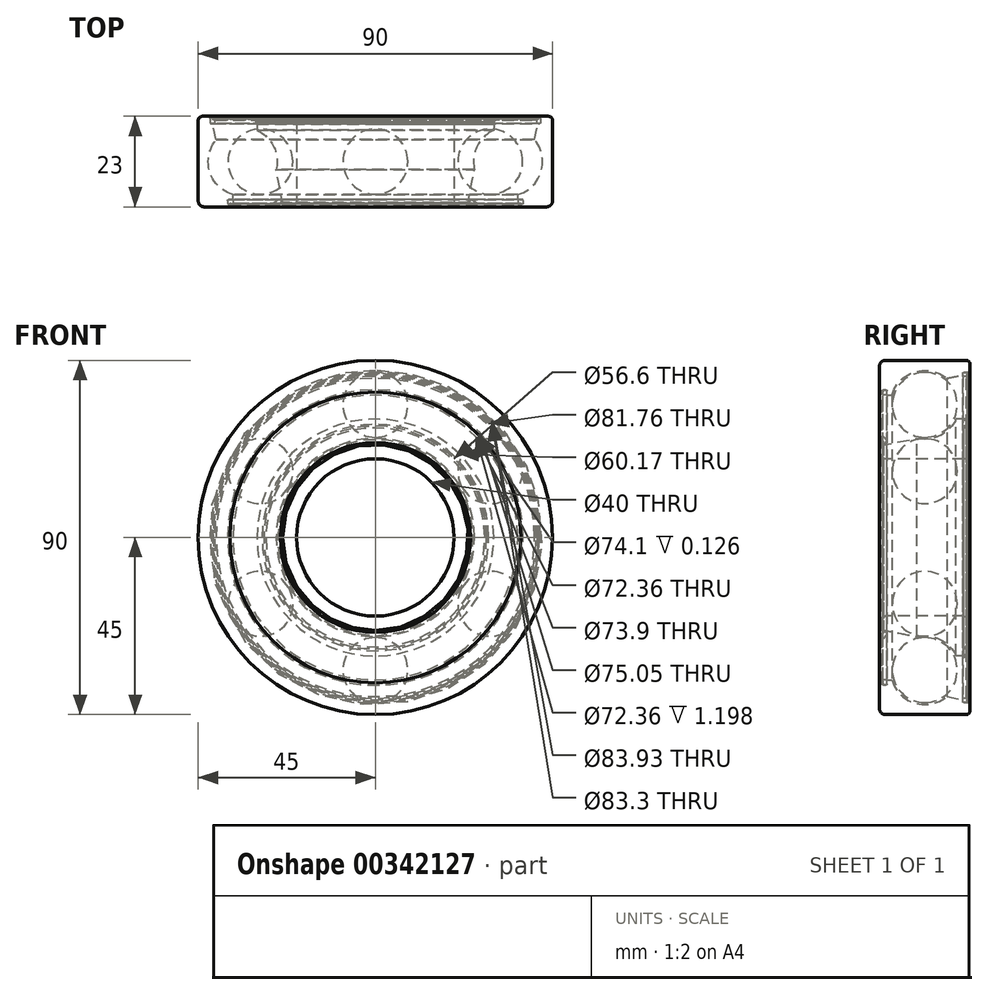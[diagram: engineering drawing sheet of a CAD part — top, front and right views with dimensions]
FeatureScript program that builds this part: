
annotation { "Feature Type Name" : "Feature", "Feature Type Description" : "" }
export const myFeature = defineFeature(function(context is Context, id is Id, definition is map)
    precondition{}
    {
        {
            var Q0;
            Q0=qCreatedBy(makeId("Right.planeOp"),FACE);
            var sketch = newSketch(context, id + "F0", { "sketchPlane" : qUnion([Q0])});
            skLineSegment(sketch, "E0", {"start": v(0, 0) * mm, "end": v(11.5, 0) * mm, "construction": true});
            skLineSegment(sketch, "E1", {"start": v(0, 0) * mm, "end": v(-11.5, 0) * mm, "construction": true});
            skLineSegment(sketch, "E2", {"start": v(-11.5, 0) * mm, "end": v(-11.5, 20) * mm, "construction": true});
            skLineSegment(sketch, "E3", {"start": v(-11.5, 37.05) * mm, "end": v(-11.5, 45) * mm});
            skLineSegment(sketch, "E4", {"start": v(-11.5, 20) * mm, "end": v(11.5, 20) * mm});
            skLineSegment(sketch, "E5", {"start": v(11.5, 45) * mm, "end": v(-11.5, 45) * mm});
            skLineSegment(sketch, "E6", {"start": v(11.5, 41.75) * mm, "end": v(11.5, 45) * mm});
            skLineSegment(sketch, "E7", {"start": v(0, 0) * mm, "end": v(0, 33.7) * mm, "construction": true});
            skLineSegment(sketch, "E8", {"start": v(0, 33.7) * mm, "end": v(28.28, 0) * mm, "construction": true});
            skArc(sketch, "E9", {"start": v(-10, 45) * mm, "mid": v(-11.06, 44.56) * mm, "end": v(-11.5, 43.5) * mm});
            skArc(sketch, "E10", {"start": v(-11.5, 21.5) * mm, "mid": v(-11.06, 20.44) * mm, "end": v(-10, 20) * mm});
            skArc(sketch, "E11", {"start": v(10, 20) * mm, "mid": v(11.06, 20.44) * mm, "end": v(11.5, 21.5) * mm});
            skArc(sketch, "E12", {"start": v(11.5, 44) * mm, "mid": v(11.2, 44.7) * mm, "end": v(10.5, 45) * mm});
            skCircle(sketch, "E13", {"center": v(0, 33.7) * mm, "radius": 8.75 * mm});
            skLineSegment(sketch, "E14", {"start": v(0, 33.7) * mm, "end": v(0, 42.46) * mm, "construction": true});
            skLineSegment(sketch, "E15", {"start": v(11.5, 27.8) * mm, "end": v(10.5, 27.8) * mm});
            skLineSegment(sketch, "E16", {"start": v(11.4, 41.65) * mm, "end": v(11.34, 41.65) * mm});
            skLineSegment(sketch, "E17", {"start": v(-11.4, 36.95) * mm, "end": v(-10.94, 36.95) * mm});
            skPoint(sketch, "E18", {"position": v(0, 65) * mm});
            skPoint(sketch, "E19", {"position": v(-11.5, 23.35) * mm});
            skLineSegment(sketch, "E20", {"start": v(-10.24, 23.6) * mm, "end": v(-10.22, 23.6) * mm});
            skLineSegment(sketch, "E21", {"start": v(-11.5, 36.95) * mm, "end": v(11.5, 41.65) * mm, "construction": true});
            skLineSegment(sketch, "E22", {"start": v(7.97, 30.09) * mm, "end": v(9.5, 30.09) * mm});
            skLineSegment(sketch, "E23", {"start": v(10, 29.59) * mm, "end": v(10, 28.4) * mm});
            skPoint(sketch, "E23.endSnap0", {"position": v(10.3, 27.8) * mm});
            skPoint(sketch, "E24.visualSharp", {"position": v(10, 30.09) * mm});
            skArc(sketch, "E24.filletArc", {"start": v(10, 29.59) * mm, "mid": v(9.85, 29.94) * mm, "end": v(9.5, 30.09) * mm});
            skPoint(sketch, "E25.newPointA", {"position": v(10, 27.8) * mm});
            skPoint(sketch, "E25.newPointB", {"position": v(9.09, 27.8) * mm});
            skArc(sketch, "E25.filletArc", {"start": v(10, 28.3) * mm, "mid": v(10.15, 27.95) * mm, "end": v(10.5, 27.8) * mm});
            skLineSegment(sketch, "E26", {"start": v(5.58, 40.44) * mm, "end": v(9.66, 41.27) * mm});
            skLineSegment(sketch, "E27", {"start": v(9.66, 41.27) * mm, "end": v(9.66, 41.65) * mm});
            skLineSegment(sketch, "E28", {"start": v(10.95, 41.97) * mm, "end": v(9.96, 41.97) * mm});
            skLineSegment(sketch, "E29", {"start": v(9.66, 41.67) * mm, "end": v(9.66, 41.65) * mm});
            skPoint(sketch, "E30.visualSharp", {"position": v(9.66, 41.97) * mm});
            skArc(sketch, "E30.filletArc", {"start": v(9.96, 41.97) * mm, "mid": v(9.75, 41.88) * mm, "end": v(9.66, 41.67) * mm});
            skPoint(sketch, "E31.visualSharp", {"position": v(11.25, 41.97) * mm});
            skArc(sketch, "E31.filletArc", {"start": v(11.25, 41.73) * mm, "mid": v(11.14, 41.9) * mm, "end": v(10.95, 41.97) * mm});
            skArc(sketch, "E32.filletArc", {"start": v(11.25, 41.73) * mm, "mid": v(11.28, 41.67) * mm, "end": v(11.34, 41.65) * mm});
            skArc(sketch, "E33.filletArc", {"start": v(11.4, 41.65) * mm, "mid": v(11.47, 41.68) * mm, "end": v(11.5, 41.75) * mm});
            skLineSegment(sketch, "E34", {"start": v(-10.84, 37.05) * mm, "end": v(-10.84, 37.23) * mm});
            skLineSegment(sketch, "E35", {"start": v(-10.54, 37.53) * mm, "end": v(-9.9, 37.53) * mm});
            skLineSegment(sketch, "E36", {"start": v(-9.6, 37.23) * mm, "end": v(-9.6, 36.95) * mm});
            skArc(sketch, "E37.filletArc", {"start": v(-11.5, 37.05) * mm, "mid": v(-11.47, 36.98) * mm, "end": v(-11.4, 36.95) * mm});
            skArc(sketch, "E38.filletArc", {"start": v(-10.94, 36.95) * mm, "mid": v(-10.87, 36.98) * mm, "end": v(-10.84, 37.05) * mm});
            skPoint(sketch, "E39.visualSharp", {"position": v(-10.84, 37.53) * mm});
            skArc(sketch, "E39.filletArc", {"start": v(-10.54, 37.53) * mm, "mid": v(-10.76, 37.44) * mm, "end": v(-10.84, 37.23) * mm});
            skPoint(sketch, "E40.visualSharp", {"position": v(-9.6, 37.53) * mm});
            skArc(sketch, "E40.filletArc", {"start": v(-9.6, 37.23) * mm, "mid": v(-9.68, 37.44) * mm, "end": v(-9.9, 37.53) * mm});
            skLineSegment(sketch, "E41", {"start": v(-9.6, 36.95) * mm, "end": v(-9.6, 36.28) * mm});
            skLineSegment(sketch, "E42", {"start": v(-9.6, 36.18) * mm, "end": v(-8.4, 36.18) * mm});
            skLineSegment(sketch, "E43", {"start": v(-11.5, 21.5) * mm, "end": v(-11.5, 23.27) * mm});
            skLineSegment(sketch, "E44", {"start": v(-10, 20) * mm, "end": v(10, 20) * mm});
            skLineSegment(sketch, "E45", {"start": v(11.5, 21.5) * mm, "end": v(11.5, 27.8) * mm});
            skLineSegment(sketch, "E46", {"start": v(-10.84, 37.05) * mm, "end": v(-10.72, 37.05) * mm});
            skLineSegment(sketch, "E47", {"start": v(-10.62, 36.95) * mm, "end": v(-10.62, 36.72) * mm});
            skLineSegment(sketch, "E48", {"start": v(-10.68, 36.63) * mm, "end": v(-11.44, 36.29) * mm});
            skLineSegment(sketch, "E49", {"start": v(-11.5, 36.2) * mm, "end": v(-11.5, 24.92) * mm});
            skLineSegment(sketch, "E50", {"start": v(-11.46, 24.84) * mm, "end": v(-10.4, 24.14) * mm});
            skLineSegment(sketch, "E51", {"start": v(-10.4, 24.14) * mm, "end": v(-10.5, 23.88) * mm});
            skLineSegment(sketch, "E52", {"start": v(-10.62, 23.52) * mm, "end": v(-10.12, 23.62) * mm});
            skLineSegment(sketch, "E53", {"start": v(-10.07, 23.7) * mm, "end": v(-9.63, 24.5) * mm});
            skLineSegment(sketch, "E54", {"start": v(-9.64, 24.6) * mm, "end": v(-10.6, 25.8) * mm});
            skLineSegment(sketch, "E55", {"start": v(-10.62, 25.86) * mm, "end": v(-10.62, 36.08) * mm});
            skLineSegment(sketch, "E56", {"start": v(-10.52, 36.18) * mm, "end": v(-9.7, 36.18) * mm});
            skPoint(sketch, "E57.visualSharp", {"position": v(-10.62, 37.05) * mm});
            skArc(sketch, "E57.filletArc", {"start": v(-10.62, 36.95) * mm, "mid": v(-10.65, 37.02) * mm, "end": v(-10.72, 37.05) * mm});
            skPoint(sketch, "E58.visualSharp", {"position": v(-10.62, 36.65) * mm});
            skArc(sketch, "E58.filletArc", {"start": v(-10.68, 36.63) * mm, "mid": v(-10.63, 36.67) * mm, "end": v(-10.62, 36.72) * mm});
            skPoint(sketch, "E59.visualSharp", {"position": v(-11.5, 36.26) * mm});
            skArc(sketch, "E59.filletArc", {"start": v(-11.44, 36.29) * mm, "mid": v(-11.48, 36.25) * mm, "end": v(-11.5, 36.2) * mm});
            skPoint(sketch, "E60.visualSharp", {"position": v(-10.62, 36.18) * mm});
            skArc(sketch, "E60.filletArc", {"start": v(-10.52, 36.18) * mm, "mid": v(-10.59, 36.15) * mm, "end": v(-10.62, 36.08) * mm});
            skPoint(sketch, "E61.visualSharp", {"position": v(-9.6, 36.18) * mm});
            skArc(sketch, "E61.filletArc", {"start": v(-9.7, 36.18) * mm, "mid": v(-9.62, 36.2) * mm, "end": v(-9.6, 36.28) * mm});
            skLineSegment(sketch, "E62", {"start": v(-9.6, 36.18) * mm, "end": v(-9.6, 36.4) * mm});
            skPoint(sketch, "E63.visualSharp", {"position": v(-11.5, 24.87) * mm});
            skArc(sketch, "E63.filletArc", {"start": v(-11.5, 24.92) * mm, "mid": v(-11.49, 24.87) * mm, "end": v(-11.46, 24.84) * mm});
            skPoint(sketch, "E64.visualSharp", {"position": v(-10.62, 25.83) * mm});
            skArc(sketch, "E64.filletArc", {"start": v(-10.62, 25.86) * mm, "mid": v(-10.61, 25.83) * mm, "end": v(-10.6, 25.8) * mm});
            skPoint(sketch, "E65.visualSharp", {"position": v(-9.6, 24.55) * mm});
            skArc(sketch, "E65.filletArc", {"start": v(-9.63, 24.5) * mm, "mid": v(-9.62, 24.55) * mm, "end": v(-9.64, 24.6) * mm});
            skPoint(sketch, "E66.newPointA", {"position": v(-10.62, 23.52) * mm});
            skArc(sketch, "E66.filletArc", {"start": v(-10.5, 23.88) * mm, "mid": v(-10.45, 23.67) * mm, "end": v(-10.24, 23.6) * mm});
            skArc(sketch, "E67.filletArc", {"start": v(-10.22, 23.6) * mm, "mid": v(-10.13, 23.64) * mm, "end": v(-10.07, 23.7) * mm});
            skLineSegment(sketch, "E68", {"start": v(-11.42, 23.37) * mm, "end": v(11.5, 27.8) * mm});
            skArc(sketch, "E69.filletArc", {"start": v(-11.42, 23.37) * mm, "mid": v(-11.48, 23.33) * mm, "end": v(-11.5, 23.27) * mm});
            skLineSegment(sketch, "E70", {"start": v(9.66, 41.27) * mm, "end": v(9.66, 40.98) * mm});
            skLineSegment(sketch, "E71", {"start": v(9.76, 40.88) * mm, "end": v(10.47, 40.88) * mm});
            skLineSegment(sketch, "E72", {"start": v(10.57, 40.78) * mm, "end": v(10.57, 30.49) * mm});
            skLineSegment(sketch, "E73", {"start": v(10.5, 30.39) * mm, "end": v(9.63, 30.2) * mm});
            skLineSegment(sketch, "E74", {"start": v(9.65, 30.09) * mm, "end": v(9.9, 30.09) * mm});
            skLineSegment(sketch, "E75", {"start": v(10, 29.99) * mm, "end": v(10, 28.3) * mm});
            skLineSegment(sketch, "E76", {"start": v(10.1, 28.3) * mm, "end": v(11.3, 28.3) * mm});
            skLineSegment(sketch, "E77", {"start": v(11.4, 28.4) * mm, "end": v(11.4, 28.68) * mm});
            skLineSegment(sketch, "E78", {"start": v(11.3, 28.78) * mm, "end": v(10.84, 28.78) * mm});
            skLineSegment(sketch, "E79", {"start": v(10.74, 28.88) * mm, "end": v(10.74, 30.05) * mm});
            skLineSegment(sketch, "E80", {"start": v(10.77, 30.12) * mm, "end": v(11.37, 30.74) * mm});
            skLineSegment(sketch, "E81", {"start": v(11.4, 30.8) * mm, "end": v(11.4, 40.89) * mm});
            skLineSegment(sketch, "E82", {"start": v(11.34, 40.98) * mm, "end": v(10.84, 41.23) * mm});
            skLineSegment(sketch, "E83", {"start": v(10.84, 41.23) * mm, "end": v(10.78, 41.29) * mm});
            skLineSegment(sketch, "E84", {"start": v(10.77, 41.43) * mm, "end": v(10.8, 41.47) * mm});
            skLineSegment(sketch, "E85", {"start": v(10.8, 41.47) * mm, "end": v(11.28, 41.68) * mm});
            skPoint(sketch, "E86.visualSharp", {"position": v(9.66, 40.88) * mm});
            skArc(sketch, "E86.filletArc", {"start": v(9.66, 40.98) * mm, "mid": v(9.69, 40.9) * mm, "end": v(9.76, 40.88) * mm});
            skPoint(sketch, "E87.visualSharp", {"position": v(10.57, 40.88) * mm});
            skArc(sketch, "E87.filletArc", {"start": v(10.57, 40.78) * mm, "mid": v(10.54, 40.85) * mm, "end": v(10.47, 40.88) * mm});
            skPoint(sketch, "E88.visualSharp", {"position": v(11.4, 40.95) * mm});
            skArc(sketch, "E88.filletArc", {"start": v(11.4, 40.89) * mm, "mid": v(11.39, 40.94) * mm, "end": v(11.34, 40.98) * mm});
            skPoint(sketch, "E89.visualSharp", {"position": v(10.7, 41.36) * mm});
            skArc(sketch, "E89.filletArc", {"start": v(10.77, 41.43) * mm, "mid": v(10.74, 41.36) * mm, "end": v(10.78, 41.29) * mm});
            skPoint(sketch, "E90.visualSharp", {"position": v(9.18, 30.09) * mm});
            skArc(sketch, "E90.filletArc", {"start": v(9.63, 30.2) * mm, "mid": v(9.6, 30.13) * mm, "end": v(9.65, 30.09) * mm});
            skArc(sketch, "E91.filletArc", {"start": v(10, 29.99) * mm, "mid": v(9.97, 30.06) * mm, "end": v(9.9, 30.09) * mm});
            skPoint(sketch, "E92.visualSharp", {"position": v(10.57, 30.4) * mm});
            skArc(sketch, "E92.filletArc", {"start": v(10.5, 30.39) * mm, "mid": v(10.55, 30.42) * mm, "end": v(10.57, 30.49) * mm});
            skPoint(sketch, "E93.visualSharp", {"position": v(10.74, 30.09) * mm});
            skArc(sketch, "E93.filletArc", {"start": v(10.77, 30.12) * mm, "mid": v(10.75, 30.09) * mm, "end": v(10.74, 30.05) * mm});
            skPoint(sketch, "E94.visualSharp", {"position": v(11.4, 30.77) * mm});
            skArc(sketch, "E94.filletArc", {"start": v(11.37, 30.74) * mm, "mid": v(11.4, 30.77) * mm, "end": v(11.4, 30.8) * mm});
            skPoint(sketch, "E95.visualSharp", {"position": v(10, 28.3) * mm});
            skArc(sketch, "E95.filletArc", {"start": v(10, 28.4) * mm, "mid": v(10.03, 28.33) * mm, "end": v(10.1, 28.3) * mm});
            skPoint(sketch, "E96.visualSharp", {"position": v(10.74, 28.78) * mm});
            skArc(sketch, "E96.filletArc", {"start": v(10.74, 28.88) * mm, "mid": v(10.77, 28.8) * mm, "end": v(10.84, 28.78) * mm});
            skPoint(sketch, "E97.visualSharp", {"position": v(11.4, 28.78) * mm});
            skArc(sketch, "E97.filletArc", {"start": v(11.4, 28.68) * mm, "mid": v(11.37, 28.75) * mm, "end": v(11.3, 28.78) * mm});
            skPoint(sketch, "E98.visualSharp", {"position": v(11.4, 28.3) * mm});
            skArc(sketch, "E98.filletArc", {"start": v(11.3, 28.3) * mm, "mid": v(11.37, 28.33) * mm, "end": v(11.4, 28.4) * mm});
            skLineSegment(sketch, "E99", {"start": v(-8.49, 31.57) * mm, "end": v(-9.58, 31.57) * mm});
            skLineSegment(sketch, "E100", {"start": v(-9.58, 31.57) * mm, "end": v(-9.58, 28.22) * mm});
            skLineSegment(sketch, "E101", {"start": v(-9.58, 28.22) * mm, "end": v(-7.74, 25.94) * mm});
            skLineSegment(sketch, "E102", {"start": v(-7.74, 25.94) * mm, "end": v(0, 26.56) * mm});
            skLineSegment(sketch, "E103", {"start": v(0, 26.56) * mm, "end": v(8.64, 35.07) * mm});
            skLineSegment(sketch, "E104", {"start": v(8.64, 35.07) * mm, "end": v(9.32, 35.07) * mm});
            skLineSegment(sketch, "E105", {"start": v(9.42, 35.17) * mm, "end": v(9.42, 39) * mm});
            skLineSegment(sketch, "E106", {"start": v(9.32, 39.1) * mm, "end": v(4.95, 39.1) * mm});
            skLineSegment(sketch, "E107", {"start": v(4.75, 38.9) * mm, "end": v(4.75, 38.22) * mm});
            skLineSegment(sketch, "E108", {"start": v(4.75, 38.22) * mm, "end": v(-8.49, 31.57) * mm});
            skPoint(sketch, "E109.visualSharp", {"position": v(9.42, 39.1) * mm});
            skArc(sketch, "E109.filletArc", {"start": v(9.42, 39) * mm, "mid": v(9.39, 39.07) * mm, "end": v(9.32, 39.1) * mm});
            skPoint(sketch, "E110.visualSharp", {"position": v(9.42, 35.07) * mm});
            skArc(sketch, "E110.filletArc", {"start": v(9.32, 35.07) * mm, "mid": v(9.39, 35.1) * mm, "end": v(9.42, 35.17) * mm});
            skPoint(sketch, "E111.visualSharp", {"position": v(4.75, 39.1) * mm});
            skArc(sketch, "E111.filletArc", {"start": v(4.95, 39.1) * mm, "mid": v(4.81, 39.04) * mm, "end": v(4.75, 38.9) * mm});
            skCircle(sketch, "E112", {"center": v(0, 33.7) * mm, "radius": 8.25 * mm});
            skLineSegment(sketch, "E113", {"start": v(0, 24.96) * mm, "end": v(0, 42.46) * mm});
            skSolve(sketch);
        }
        {
            var Q0;
            Q0=makeQuery(id+"F0.imprint","IMPRINT",FACE,{"disambiguationData":[TD([[makeQuery(id+"F0.imprint","IMPRINT",EDGE,{"derivedFrom":sQuery(id+"F0.wireOp",EDGE,"E10")}),1.0]])]});
            var Q1;
            {var subQ1=sQuery(id+"F0.wireOp",EDGE,"E15");Q1=makeQuery(id+"F0.imprint","IMPRINT",FACE,{"disambiguationData":[TD([[makeQuery(id+"F0.imprint","IMPRINT",EDGE,{"derivedFrom":subQ1}),1.0]])]});}
            var Q2;
            Q2=sQuery(id+"F0.wireOp",EDGE,"E0");
            revolve(context, id + "F1", {"entities" : qUnion([Q0, Q1]), "axis" : qUnion([Q2]), "revolveType" : RevolveType.FULL});
        }
        {
            var Q0;
            {var subQ1=sQuery(id+"F0.wireOp",EDGE,"E99");Q0=makeQuery(id+"F0.imprint","IMPRINT",FACE,{"disambiguationData":[TD([[makeQuery(id+"F0.imprint","IMPRINT",EDGE,{"derivedFrom":subQ1}),1.0]])]});}
            var Q1;
            {var subQ0=sQuery(id+"F0.wireOp",EDGE,"E107");Q1=makeQuery(id+"F0.imprint","IMPRINT",FACE,{"disambiguationData":[TD([[makeQuery(id+"F0.imprint","IMPRINT",EDGE,{"derivedFrom":subQ0}),1.0]])]});}
            var Q2;
            {var subQ4=sQuery(id+"F0.wireOp",EDGE,"E104");Q2=makeQuery(id+"F0.imprint","IMPRINT",FACE,{"disambiguationData":[TD([[makeQuery(id+"F0.imprint","IMPRINT",EDGE,{"derivedFrom":subQ4}),1.0]])]});}
            var Q3;
            {var subQ1=sQuery(id+"F0.wireOp",EDGE,"E13");var subQ3=sQuery(id+"F0.wireOp",EDGE,"E106");var subQ4=makeQuery(id+"F0.imprint","INTERSECT",VERTEX,{"derivedFrom":[subQ1,subQ3]});Q3=makeQuery(id+"F0.imprint","IMPRINT",FACE,{"disambiguationData":[TD([[makeQuery(id+"F0.imprint","IMPRINT",EDGE,{"disambiguationData":[TD([[subQ4,-1.0]])],"derivedFrom":subQ3}),1.0]])]});}
            var Q4;
            {var subQ0=sQuery(id+"F0.wireOp",EDGE,"E113");var subQ5=sQuery(id+"F0.wireOp",EDGE,"E108");var subQ6=makeQuery(id+"F0.imprint","INTERSECT",VERTEX,{"derivedFrom":[subQ5,subQ0]});Q4=makeQuery(id+"F0.imprint","IMPRINT",FACE,{"disambiguationData":[TD([[makeQuery(id+"F0.imprint","IMPRINT",EDGE,{"disambiguationData":[TD([[subQ6,-1.0]])],"derivedFrom":subQ5}),1.0]])]});}
            var Q5;
            {var subQ1=sQuery(id+"F0.wireOp",EDGE,"E13");var subQ3=sQuery(id+"F0.wireOp",EDGE,"E102");var subQ4=makeQuery(id+"F0.imprint","INTERSECT",VERTEX,{"derivedFrom":[subQ1,subQ3]});Q5=makeQuery(id+"F0.imprint","IMPRINT",FACE,{"disambiguationData":[TD([[makeQuery(id+"F0.imprint","IMPRINT",EDGE,{"disambiguationData":[TD([[subQ4,-1.0]])],"derivedFrom":subQ3}),1.0]])]});}
            var Q6;
            Q6=sQuery(id+"F0.wireOp",EDGE,"E1");
            revolve(context, id + "F2", {"entities" : qUnion([Q0, Q1, Q2, Q3, Q4, Q5]), "axis" : qUnion([Q6]), "revolveType" : RevolveType.FULL});
        }
        {
            var Q0;
            {var subQ2=sQuery(id+"F0.wireOp",EDGE,"E107");Q0=makeQuery(id+"F0.imprint","IMPRINT",FACE,{"disambiguationData":[TD([[makeQuery(id+"F0.imprint","IMPRINT",EDGE,{"derivedFrom":subQ2}),-1.0]])]});}
            var Q1;
            {var subQ5=sQuery(id+"F0.wireOp",EDGE,"E13");var subQ6=makeQuery(id+"F0.imprint","INTERSECT",VERTEX,{"derivedFrom":[subQ5,sQuery(id+"F0.wireOp",EDGE,"E26")]});Q1=makeQuery(id+"F0.imprint","IMPRINT",FACE,{"disambiguationData":[TD([[makeQuery(id+"F0.imprint","IMPRINT",EDGE,{"disambiguationData":[TD([[subQ6,1.0]])],"derivedFrom":subQ5}),1.0]])]});}
            var Q2;
            {var subQ1=sQuery(id+"F0.wireOp",EDGE,"E13");var subQ3=sQuery(id+"F0.wireOp",EDGE,"E106");var subQ4=makeQuery(id+"F0.imprint","INTERSECT",VERTEX,{"derivedFrom":[subQ1,subQ3]});Q2=makeQuery(id+"F0.imprint","IMPRINT",FACE,{"disambiguationData":[TD([[makeQuery(id+"F0.imprint","IMPRINT",EDGE,{"disambiguationData":[TD([[subQ4,-1.0]])],"derivedFrom":subQ3}),1.0]])]});}
            var Q3;
            {var subQ1=sQuery(id+"F0.wireOp",EDGE,"E107");Q3=makeQuery(id+"F0.imprint","IMPRINT",FACE,{"disambiguationData":[TD([[makeQuery(id+"F0.imprint","IMPRINT",EDGE,{"derivedFrom":subQ1}),1.0]])]});}
            var Q4;
            {var subQ1=sQuery(id+"F0.wireOp",EDGE,"E13");var subQ5=makeQuery(id+"F0.imprint","INTERSECT",VERTEX,{"derivedFrom":[subQ1,sQuery(id+"F0.wireOp",EDGE,"E22")]});Q4=makeQuery(id+"F0.imprint","IMPRINT",FACE,{"disambiguationData":[TD([[makeQuery(id+"F0.imprint","IMPRINT",EDGE,{"disambiguationData":[TD([[subQ5,1.0]])],"derivedFrom":subQ1}),1.0]])]});}
            var Q5;
            {var subQ0=sQuery(id+"F0.wireOp",EDGE,"E113");var subQ1=sQuery(id+"F0.wireOp",EDGE,"E13");var subQ2=makeQuery(id+"F0.imprint","INTERSECT",VERTEX,{"disambiguationData":[OD(0.0)],"derivedFrom":[subQ1,subQ0]});Q5=makeQuery(id+"F0.imprint","IMPRINT",FACE,{"disambiguationData":[TD([[makeQuery(id+"F0.imprint","IMPRINT",EDGE,{"disambiguationData":[TD([[subQ2,-1.0]])],"derivedFrom":subQ1}),1.0]])]});}
            var Q6;
            {var subQ0=sQuery(id+"F0.wireOp",EDGE,"E113");var subQ1=sQuery(id+"F0.wireOp",EDGE,"E68");var subQ2=makeQuery(id+"F0.imprint","INTERSECT",VERTEX,{"derivedFrom":[subQ1,subQ0]});Q6=makeQuery(id+"F0.imprint","IMPRINT",FACE,{"disambiguationData":[TD([[makeQuery(id+"F0.imprint","IMPRINT",EDGE,{"disambiguationData":[TD([[subQ2,-1.0]])],"derivedFrom":subQ1}),-1.0]])]});}
            var Q7;
            {var subQ0=sQuery(id+"F0.wireOp",EDGE,"E113");var subQ1=sQuery(id+"F0.wireOp",EDGE,"E68");var subQ2=makeQuery(id+"F0.imprint","INTERSECT",VERTEX,{"derivedFrom":[subQ1,subQ0]});Q7=makeQuery(id+"F0.imprint","IMPRINT",FACE,{"disambiguationData":[TD([[makeQuery(id+"F0.imprint","IMPRINT",EDGE,{"disambiguationData":[TD([[subQ2,-1.0]])],"derivedFrom":subQ1}),1.0]])]});}
            var Q8;
            Q8=sQuery(id+"F0.wireOp",EDGE,"E113");
            revolve(context, id + "F3", {"operationType" : NewBodyOperationType.ADD, "entities" : qUnion([Q0, Q1, Q2, Q3, Q4, Q5, Q6, Q7]), "axis" : qUnion([Q8]), "revolveType" : RevolveType.FULL});
        }
        {
            var Q0;
            Q0=makeQuery(id+"F3.opRevolve","SWEPT_BODY",BODY,{"disambiguationData":[OSD([sQuery(id+"F0.wireOp",EDGE,"E13"),sQuery(id+"F0.wireOp",EDGE,"E113")])]});
            var Q1;
            Q1=sQuery(id+"F0.wireOp",EDGE,"E1");
            circularPattern(context, id + "F4", {"operationType" : NewBodyOperationType.REMOVE, "entities" : qUnion([Q0]), "axis" : qUnion([Q1]), "angle" : 360 * degree, "instanceCount" : 6, "equalSpace" : true});
        }
        {
            var Q0;
            {var subQ2=sQuery(id+"F0.wireOp",EDGE,"E107");Q0=makeQuery(id+"F0.imprint","IMPRINT",FACE,{"disambiguationData":[TD([[makeQuery(id+"F0.imprint","IMPRINT",EDGE,{"derivedFrom":subQ2}),-1.0]])]});}
            var Q1;
            {var subQ1=sQuery(id+"F0.wireOp",EDGE,"E107");Q1=makeQuery(id+"F0.imprint","IMPRINT",FACE,{"disambiguationData":[TD([[makeQuery(id+"F0.imprint","IMPRINT",EDGE,{"derivedFrom":subQ1}),1.0]])]});}
            var Q2;
            {var subQ0=sQuery(id+"F0.wireOp",EDGE,"E113");var subQ1=sQuery(id+"F0.wireOp",EDGE,"E68");var subQ2=makeQuery(id+"F0.imprint","INTERSECT",VERTEX,{"derivedFrom":[subQ1,subQ0]});Q2=makeQuery(id+"F0.imprint","IMPRINT",FACE,{"disambiguationData":[TD([[makeQuery(id+"F0.imprint","IMPRINT",EDGE,{"disambiguationData":[TD([[subQ2,-1.0]])],"derivedFrom":subQ1}),1.0]])]});}
            var Q3;
            {var subQ0=sQuery(id+"F0.wireOp",EDGE,"E113");var subQ1=sQuery(id+"F0.wireOp",EDGE,"E68");var subQ2=makeQuery(id+"F0.imprint","INTERSECT",VERTEX,{"derivedFrom":[subQ1,subQ0]});Q3=makeQuery(id+"F0.imprint","IMPRINT",FACE,{"disambiguationData":[TD([[makeQuery(id+"F0.imprint","IMPRINT",EDGE,{"disambiguationData":[TD([[subQ2,-1.0]])],"derivedFrom":subQ1}),-1.0]])]});}
            var Q4;
            Q4=sQuery(id+"F0.wireOp",EDGE,"E113");
            revolve(context, id + "F5", {"entities" : qUnion([Q0, Q1, Q2, Q3]), "axis" : qUnion([Q4]), "revolveType" : RevolveType.FULL});
        }
        {
            var Q0;
            Q0=makeQuery(id+"F5.opRevolve","SWEPT_BODY",BODY,{"disambiguationData":[OSD([sQuery(id+"F0.wireOp",EDGE,"E112"),sQuery(id+"F0.wireOp",EDGE,"E113")])]});
            var Q1;
            Q1=sQuery(id+"F0.wireOp",EDGE,"E1");
            circularPattern(context, id + "F6", {"entities" : qUnion([Q0]), "axis" : qUnion([Q1]), "angle" : 360 * degree, "instanceCount" : 6, "equalSpace" : true});
        }
        {
            var Q0;
            {var subQ6=sQuery(id+"F0.wireOp",EDGE,"E9");Q0=makeQuery(id+"F0.imprint","IMPRINT",FACE,{"disambiguationData":[TD([[makeQuery(id+"F0.imprint","IMPRINT",EDGE,{"derivedFrom":subQ6}),1.0]])]});}
            var Q1;
            Q1=sQuery(id+"F0.wireOp",EDGE,"E1");
            revolve(context, id + "F7", {"entities" : qUnion([Q0]), "axis" : qUnion([Q1]), "revolveType" : RevolveType.FULL});
        }
        {
            var Q0;
            Q0=makeQuery(id+"F0.imprint","IMPRINT",FACE,{"disambiguationData":[TD([[makeQuery(id+"F0.imprint","IMPRINT",EDGE,{"derivedFrom":sQuery(id+"F0.wireOp",EDGE,"E34")}),-1.0]])]});
            var Q1;
            Q1=makeQuery(id+"F0.imprint","IMPRINT",FACE,{"disambiguationData":[TD([[makeQuery(id+"F0.imprint","IMPRINT",EDGE,{"derivedFrom":sQuery(id+"F0.wireOp",EDGE,"E27")}),-1.0]])]});
            var Q2;
            Q2=sQuery(id+"F0.wireOp",EDGE,"E0");
            revolve(context, id + "F8", {"entities" : qUnion([Q0, Q1]), "axis" : qUnion([Q2]), "revolveType" : RevolveType.FULL});
        }
    });
